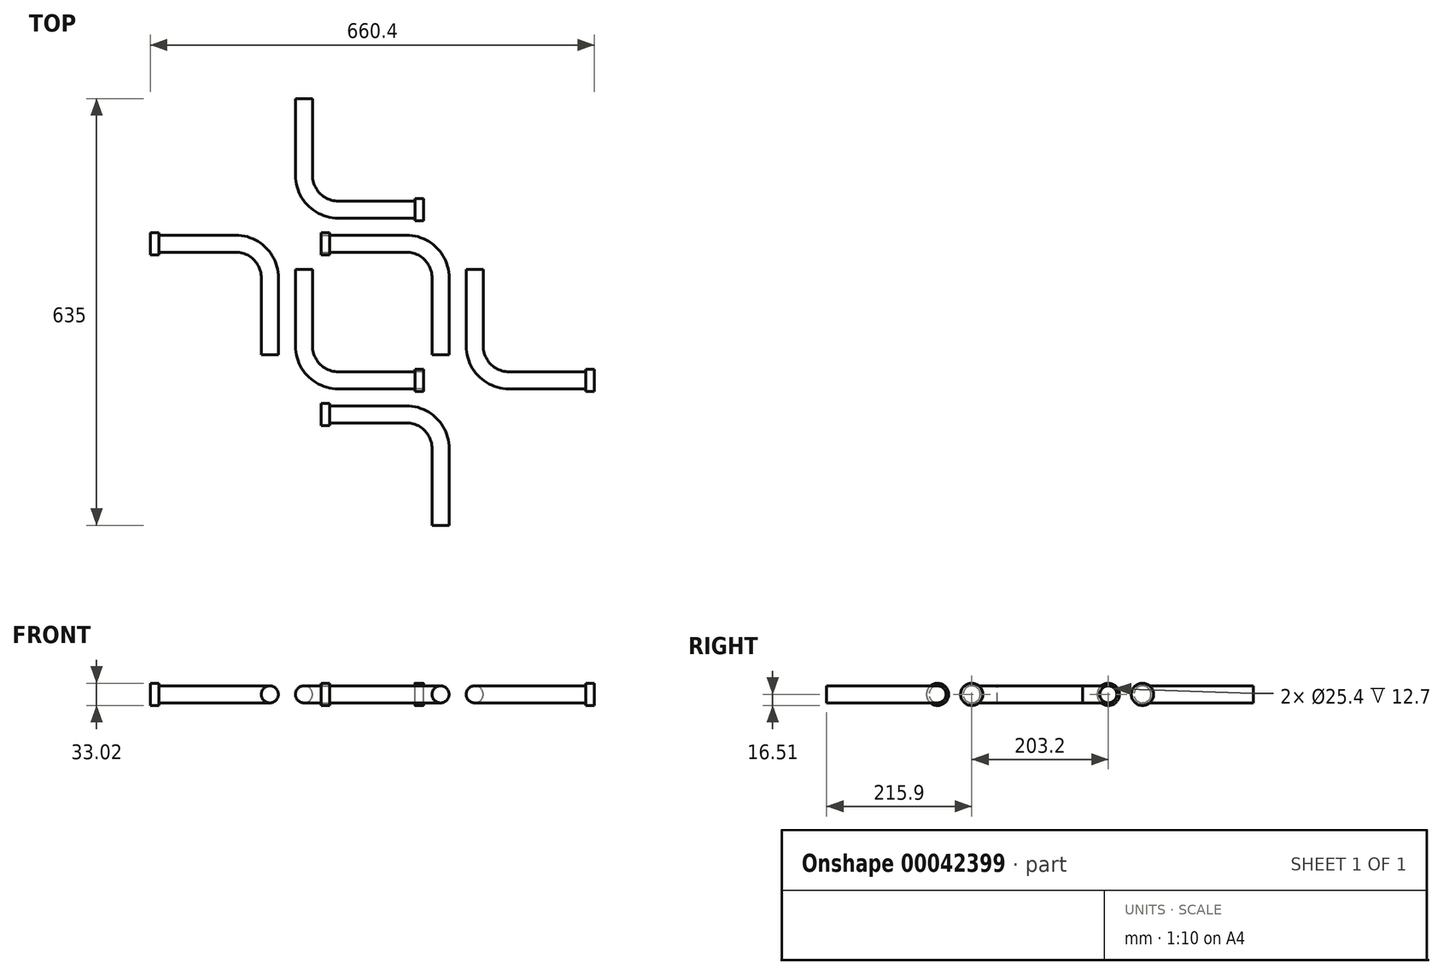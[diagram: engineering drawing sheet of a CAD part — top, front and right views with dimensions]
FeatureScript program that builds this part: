
annotation { "Feature Type Name" : "Feature", "Feature Type Description" : "" }
export const myFeature = defineFeature(function(context is Context, id is Id, definition is map)
    precondition{}
    {
        {
            var Q0;
            Q0=qCreatedBy(makeId("Top.planeOp"),FACE);
            var sketch = newSketch(context, id + "F0", { "sketchPlane" : qUnion([Q0])});
            skLineSegment(sketch, "E0.bottom", {"start": v(-127, 127) * mm, "end": v(127, 127) * mm});
            skLineSegment(sketch, "E0.top", {"start": v(-127, -127) * mm, "end": v(127, -127) * mm});
            skLineSegment(sketch, "E0.left", {"start": v(-127, 127) * mm, "end": v(-127, -127) * mm});
            skLineSegment(sketch, "E0.right", {"start": v(127, 127) * mm, "end": v(127, -127) * mm});
            skLineSegment(sketch, "E1", {"start": v(63.5, 152.4) * mm, "end": v(-50.8, 152.4) * mm});
            skLineSegment(sketch, "E2", {"start": v(-101.6, 203.2) * mm, "end": v(-101.6, 317.5) * mm});
            skLineSegment(sketch, "E3", {"start": v(-127, -127) * mm, "end": v(127, 127) * mm});
            skLineSegment(sketch, "E4", {"start": v(-127, 127) * mm, "end": v(127, -127) * mm});
            skLineSegment(sketch, "E5", {"start": v(-63.5, 101.6) * mm, "end": v(50.8, 101.6) * mm});
            skLineSegment(sketch, "E6", {"start": v(101.6, 50.8) * mm, "end": v(101.6, -63.5) * mm});
            skPoint(sketch, "E7.visualSharp", {"position": v(101.6, 101.6) * mm});
            skArc(sketch, "E7.filletArc", {"start": v(101.6, 50.8) * mm, "mid": v(86.72, 86.72) * mm, "end": v(50.8, 101.6) * mm});
            skLineSegment(sketch, "E8.bottom", {"start": v(-139.7, 139.7) * mm, "end": v(139.7, 139.7) * mm});
            skLineSegment(sketch, "E8.top", {"start": v(-139.7, -163.3) * mm, "end": v(139.7, -163.3) * mm});
            skLineSegment(sketch, "E8.left", {"start": v(-139.7, 139.7) * mm, "end": v(-139.7, -163.3) * mm});
            skLineSegment(sketch, "E8.right", {"start": v(139.7, 139.7) * mm, "end": v(139.7, -163.3) * mm});
            skPoint(sketch, "E9.visualSharp", {"position": v(-101.6, 152.4) * mm});
            skArc(sketch, "E9.filletArc", {"start": v(-101.6, 203.2) * mm, "mid": v(-86.72, 167.28) * mm, "end": v(-50.8, 152.4) * mm});
            skSolve(sketch);
        }
        {
            var Q0;
            Q0=sQuery(id+"F0.wireOp",VERTEX,"E2.end");
            var Q1;
            Q1=qCreatedBy(makeId("Front.planeOp"),FACE);
            cPlane(context, id + "F1", {"entities" : qUnion([Q0, Q1]), "cplaneType" : CPlaneType.PLANE_POINT, "offset" : 152.4 * mm, "width" : 152.4 * mm, "height" : 152.4 * mm});
        }
        {
            var Q0;
            Q0=qCreatedBy(id+"F1.planeOp",FACE);
            var sketch = newSketch(context, id + "F2", { "sketchPlane" : qUnion([Q0])});
            skCircle(sketch, "E10", {"center": v(-101.6, 0) * mm, "radius": 12.7 * mm});
            skSolve(sketch);
        }
        {
            var Q0;
            Q0=makeQuery(id+"F2.imprint","IMPRINT",FACE,{"disambiguationData":[TD([[makeQuery(id+"F2.imprint","IMPRINT",EDGE,{"derivedFrom":sQuery(id+"F2.wireOp",EDGE,"E10")}),1.0]])]});
            var Q1;
            Q1=sQuery(id+"F0.wireOp",EDGE,"E2");
            var Q2;
            Q2=sQuery(id+"F0.wireOp",EDGE,"E9.filletArc");
            var Q3;
            Q3=sQuery(id+"F0.wireOp",EDGE,"E1");
            sweep(context, id + "F3", {"profiles" : qUnion([Q0]), "path" : qUnion([Q1, Q2, Q3])});
        }
        {
            var Q0;
            Q0=sQuery(id+"F0.wireOp",EDGE,"E3");
            cPlane(context, id + "F4", {"entities" : qUnion([Q0]), "cplaneType" : CPlaneType.LINE_ANGLE, "offset" : 152.4 * mm, "angle" : 90 * degree, "width" : 152.4 * mm, "height" : 152.4 * mm});
        }
        {
            var Q0;
            Q0=makeQuery(id+"F3.opSweep","SWEPT_BODY",BODY,{"disambiguationData":[OSD([sQuery(id+"F0.wireOp",EDGE,"E1"),sQuery(id+"F2.wireOp",EDGE,"E10")])]});
            var Q1;
            Q1=qCreatedBy(id+"F4.planeOp",FACE);
            mirror(context, id + "F5", {"entities" : qUnion([Q0]), "mirrorPlane" : qUnion([Q1])});
        }
        {
            var Q0;
            Q0=sQuery(id+"F0.wireOp",EDGE,"E4");
            cPlane(context, id + "F6", {"entities" : qUnion([Q0]), "cplaneType" : CPlaneType.LINE_ANGLE, "offset" : 152.4 * mm, "angle" : 90 * degree, "width" : 152.4 * mm, "height" : 152.4 * mm});
        }
        {
            var Q0;
            Q0=makeQuery(id+"F3.opSweep","SWEPT_BODY",BODY,{"disambiguationData":[OSD([sQuery(id+"F0.wireOp",EDGE,"E1"),sQuery(id+"F2.wireOp",EDGE,"E10")])]});
            var Q1;
            Q1=makeQuery(id+"F5.opPattern","COPY",BODY,{"derivedFrom":makeQuery(id+"F3.opSweep","SWEPT_BODY",BODY,{"disambiguationData":[OSD([sQuery(id+"F0.wireOp",EDGE,"E1"),sQuery(id+"F2.wireOp",EDGE,"E10")])]}),"instanceName":"1"});
            var Q2;
            Q2=qCreatedBy(id+"F6.planeOp",FACE);
            mirror(context, id + "F7", {"entities" : qUnion([Q0, Q1]), "mirrorPlane" : qUnion([Q2])});
        }
        {
            var Q0;
            Q0=qCreatedBy(makeId("Front.planeOp"),FACE);
            var Q1;
            Q1=sQuery(id+"F0.wireOp",VERTEX,"E6.end");
            cPlane(context, id + "F8", {"entities" : qUnion([Q0, Q1]), "cplaneType" : CPlaneType.PLANE_POINT, "offset" : 152.4 * mm, "width" : 152.4 * mm, "height" : 152.4 * mm});
        }
        {
            var Q0;
            Q0=qCreatedBy(id+"F8.planeOp",FACE);
            var sketch = newSketch(context, id + "F9", { "sketchPlane" : qUnion([Q0])});
            skCircle(sketch, "E11", {"center": v(101.6, 0) * mm, "radius": 12.7 * mm});
            skSolve(sketch);
        }
        {
            var Q0;
            Q0=makeQuery(id+"F9.imprint","IMPRINT",FACE,{"disambiguationData":[TD([[makeQuery(id+"F9.imprint","IMPRINT",EDGE,{"derivedFrom":sQuery(id+"F9.wireOp",EDGE,"E11")}),1.0]])]});
            var Q1;
            Q1=sQuery(id+"F0.wireOp",EDGE,"E6");
            var Q2;
            Q2=sQuery(id+"F0.wireOp",EDGE,"E7.filletArc");
            var Q3;
            Q3=sQuery(id+"F0.wireOp",EDGE,"E5");
            sweep(context, id + "F10", {"profiles" : qUnion([Q0]), "path" : qUnion([Q1, Q2, Q3])});
        }
        {
            var Q0;
            Q0=makeQuery(id+"F10.opSweep","SWEPT_BODY",BODY,{"disambiguationData":[OSD([sQuery(id+"F0.wireOp",EDGE,"E5"),sQuery(id+"F9.wireOp",EDGE,"E11")])]});
            var Q1;
            Q1=qCreatedBy(id+"F6.planeOp",FACE);
            mirror(context, id + "F11", {"entities" : qUnion([Q0]), "mirrorPlane" : qUnion([Q1])});
        }
        {
            var Q0;
            Q0=makeQuery(id+"F3.opSweep","CAP_FACE",FACE,{"disambiguationData":[OSD([sQuery(id+"F0.wireOp",VERTEX,"E1.start"),sQuery(id+"F2.wireOp",EDGE,"E10")])],"isStart":false});
            var sketch = newSketch(context, id + "F12", { "sketchPlane" : qUnion([Q0])});
            skCircle(sketch, "E12", {"center": v(152.4, 0) * mm, "radius": 16.51 * mm});
            skSolve(sketch);
        }
        {
            var Q0;
            Q0=makeQuery(id+"F12.imprint","IMPRINT",FACE,{"disambiguationData":[TD([[makeQuery(id+"F12.imprint","IMPRINT",EDGE,{"derivedFrom":sQuery(id+"F12.wireOp",EDGE,"E12")}),1.0]])]});
            var Q1;
            Q1=makeQuery(id+"F12.imprint","IMPRINT",FACE,{"disambiguationData":[TD([[makeQuery(id+"F12.imprint","IMPRINT",EDGE,{"derivedFrom":makeQuery(id+"F3.opSweep","CAP_EDGE",EDGE,{"disambiguationData":[OSD([sQuery(id+"F0.wireOp",VERTEX,"E1.start"),sQuery(id+"F2.wireOp",EDGE,"E10")])],"isStart":false})}),1.0]])]});
            extrude(context, id + "F13", {"entities" : qUnion([Q0, Q1]), "depth" : 12.7 * mm});
        }
        {
            var Q0;
            Q0=makeQuery(id+"F5.opPattern","COPY",FACE,{"derivedFrom":makeQuery(id+"F3.opSweep","CAP_FACE",FACE,{"disambiguationData":[OSD([sQuery(id+"F0.wireOp",VERTEX,"E2.end"),sQuery(id+"F2.wireOp",EDGE,"E10")])],"isStart":true}),"instanceName":"1"});
            var sketch = newSketch(context, id + "F14", { "sketchPlane" : qUnion([Q0])});
            skCircle(sketch, "E13", {"center": v(-101.6, 0) * mm, "radius": 16.51 * mm});
            skSolve(sketch);
        }
        {
            var Q0;
            Q0=makeQuery(id+"F14.imprint","IMPRINT",FACE,{"disambiguationData":[TD([[makeQuery(id+"F14.imprint","IMPRINT",EDGE,{"derivedFrom":makeQuery(id+"F5.opPattern","COPY",EDGE,{"derivedFrom":makeQuery(id+"F3.opSweep","CAP_EDGE",EDGE,{"disambiguationData":[OSD([sQuery(id+"F0.wireOp",VERTEX,"E2.end"),sQuery(id+"F2.wireOp",EDGE,"E10")])],"isStart":true}),"instanceName":"1"})}),1.0]])]});
            var Q1;
            Q1=makeQuery(id+"F14.imprint","IMPRINT",FACE,{"disambiguationData":[TD([[makeQuery(id+"F14.imprint","IMPRINT",EDGE,{"derivedFrom":sQuery(id+"F14.wireOp",EDGE,"E13")}),1.0]])]});
            extrude(context, id + "F15", {"entities" : qUnion([Q0, Q1]), "depth" : 12.7 * mm});
        }
        {
            var Q0;
            Q0=makeQuery(id+"F11.opPattern","COPY",FACE,{"derivedFrom":makeQuery(id+"F10.opSweep","CAP_FACE",FACE,{"disambiguationData":[OSD([sQuery(id+"F0.wireOp",VERTEX,"E6.end"),sQuery(id+"F9.wireOp",EDGE,"E11")])],"isStart":true}),"instanceName":"1"});
            var sketch = newSketch(context, id + "F16", { "sketchPlane" : qUnion([Q0])});
            skCircle(sketch, "E14", {"center": v(-101.6, 0) * mm, "radius": 16.51 * mm});
            skSolve(sketch);
        }
        {
            var Q0;
            Q0=makeQuery(id+"F16.imprint","IMPRINT",FACE,{"disambiguationData":[TD([[makeQuery(id+"F16.imprint","IMPRINT",EDGE,{"derivedFrom":makeQuery(id+"F11.opPattern","COPY",EDGE,{"derivedFrom":makeQuery(id+"F10.opSweep","CAP_EDGE",EDGE,{"disambiguationData":[OSD([sQuery(id+"F0.wireOp",VERTEX,"E6.end"),sQuery(id+"F9.wireOp",EDGE,"E11")])],"isStart":true}),"instanceName":"1"})}),-1.0]])]});
            var Q1;
            Q1=makeQuery(id+"F16.imprint","IMPRINT",FACE,{"disambiguationData":[TD([[makeQuery(id+"F16.imprint","IMPRINT",EDGE,{"derivedFrom":sQuery(id+"F16.wireOp",EDGE,"E14")}),1.0]])]});
            extrude(context, id + "F17", {"entities" : qUnion([Q0, Q1]), "depth" : 12.7 * mm});
        }
        {
            var Q0;
            Q0=makeQuery(id+"F7.opPattern","COPY",FACE,{"derivedFrom":makeQuery(id+"F5.opPattern","COPY",FACE,{"derivedFrom":makeQuery(id+"F3.opSweep","CAP_FACE",FACE,{"disambiguationData":[OSD([sQuery(id+"F0.wireOp",VERTEX,"E1.start"),sQuery(id+"F2.wireOp",EDGE,"E10")])],"isStart":false}),"instanceName":"1"}),"instanceName":"1"});
            var sketch = newSketch(context, id + "F18", { "sketchPlane" : qUnion([Q0])});
            skCircle(sketch, "E15", {"center": v(152.4, 0) * mm, "radius": 16.51 * mm});
            skSolve(sketch);
        }
        {
            var Q0;
            Q0=makeQuery(id+"F18.imprint","IMPRINT",FACE,{"disambiguationData":[TD([[makeQuery(id+"F18.imprint","IMPRINT",EDGE,{"derivedFrom":makeQuery(id+"F7.opPattern","COPY",EDGE,{"derivedFrom":makeQuery(id+"F5.opPattern","COPY",EDGE,{"derivedFrom":makeQuery(id+"F3.opSweep","CAP_EDGE",EDGE,{"disambiguationData":[OSD([sQuery(id+"F0.wireOp",VERTEX,"E1.start"),sQuery(id+"F2.wireOp",EDGE,"E10")])],"isStart":false}),"instanceName":"1"}),"instanceName":"1"})}),1.0]])]});
            var Q1;
            Q1=makeQuery(id+"F18.imprint","IMPRINT",FACE,{"disambiguationData":[TD([[makeQuery(id+"F18.imprint","IMPRINT",EDGE,{"derivedFrom":sQuery(id+"F18.wireOp",EDGE,"E15")}),1.0]])]});
            extrude(context, id + "F19", {"entities" : qUnion([Q0, Q1]), "depth" : 12.7 * mm});
        }
        {
            var Q0;
            Q0=makeQuery(id+"F7.opPattern","COPY",FACE,{"derivedFrom":makeQuery(id+"F3.opSweep","CAP_FACE",FACE,{"disambiguationData":[OSD([sQuery(id+"F0.wireOp",VERTEX,"E2.end"),sQuery(id+"F2.wireOp",EDGE,"E10")])],"isStart":true}),"instanceName":"1"});
            var sketch = newSketch(context, id + "F20", { "sketchPlane" : qUnion([Q0])});
            skCircle(sketch, "E16", {"center": v(-101.6, 0) * mm, "radius": 16.51 * mm});
            skSolve(sketch);
        }
        {
            var Q0;
            Q0=makeQuery(id+"F20.imprint","IMPRINT",FACE,{"disambiguationData":[TD([[makeQuery(id+"F20.imprint","IMPRINT",EDGE,{"derivedFrom":makeQuery(id+"F7.opPattern","COPY",EDGE,{"derivedFrom":makeQuery(id+"F3.opSweep","CAP_EDGE",EDGE,{"disambiguationData":[OSD([sQuery(id+"F0.wireOp",VERTEX,"E2.end"),sQuery(id+"F2.wireOp",EDGE,"E10")])],"isStart":true}),"instanceName":"1"})}),1.0]])]});
            var Q1;
            Q1=makeQuery(id+"F20.imprint","IMPRINT",FACE,{"disambiguationData":[TD([[makeQuery(id+"F20.imprint","IMPRINT",EDGE,{"derivedFrom":sQuery(id+"F20.wireOp",EDGE,"E16")}),1.0]])]});
            extrude(context, id + "F21", {"entities" : qUnion([Q0, Q1]), "depth" : 12.7 * mm});
        }
        {
            var Q0;
            Q0=makeQuery(id+"F10.opSweep","CAP_FACE",FACE,{"disambiguationData":[OSD([sQuery(id+"F0.wireOp",VERTEX,"E5.start"),sQuery(id+"F9.wireOp",EDGE,"E11")])],"isStart":false});
            var sketch = newSketch(context, id + "F22", { "sketchPlane" : qUnion([Q0])});
            skCircle(sketch, "E17", {"center": v(-101.6, 0) * mm, "radius": 16.51 * mm});
            skSolve(sketch);
        }
        {
            var Q0;
            Q0=makeQuery(id+"F22.imprint","IMPRINT",FACE,{"disambiguationData":[TD([[makeQuery(id+"F22.imprint","IMPRINT",EDGE,{"derivedFrom":makeQuery(id+"F10.opSweep","CAP_EDGE",EDGE,{"disambiguationData":[OSD([sQuery(id+"F0.wireOp",VERTEX,"E5.start"),sQuery(id+"F9.wireOp",EDGE,"E11")])],"isStart":false})}),-1.0]])]});
            var Q1;
            Q1=makeQuery(id+"F22.imprint","IMPRINT",FACE,{"disambiguationData":[TD([[makeQuery(id+"F22.imprint","IMPRINT",EDGE,{"derivedFrom":sQuery(id+"F22.wireOp",EDGE,"E17")}),1.0]])]});
            extrude(context, id + "F23", {"entities" : qUnion([Q0, Q1]), "depth" : 12.7 * mm});
        }
    });
